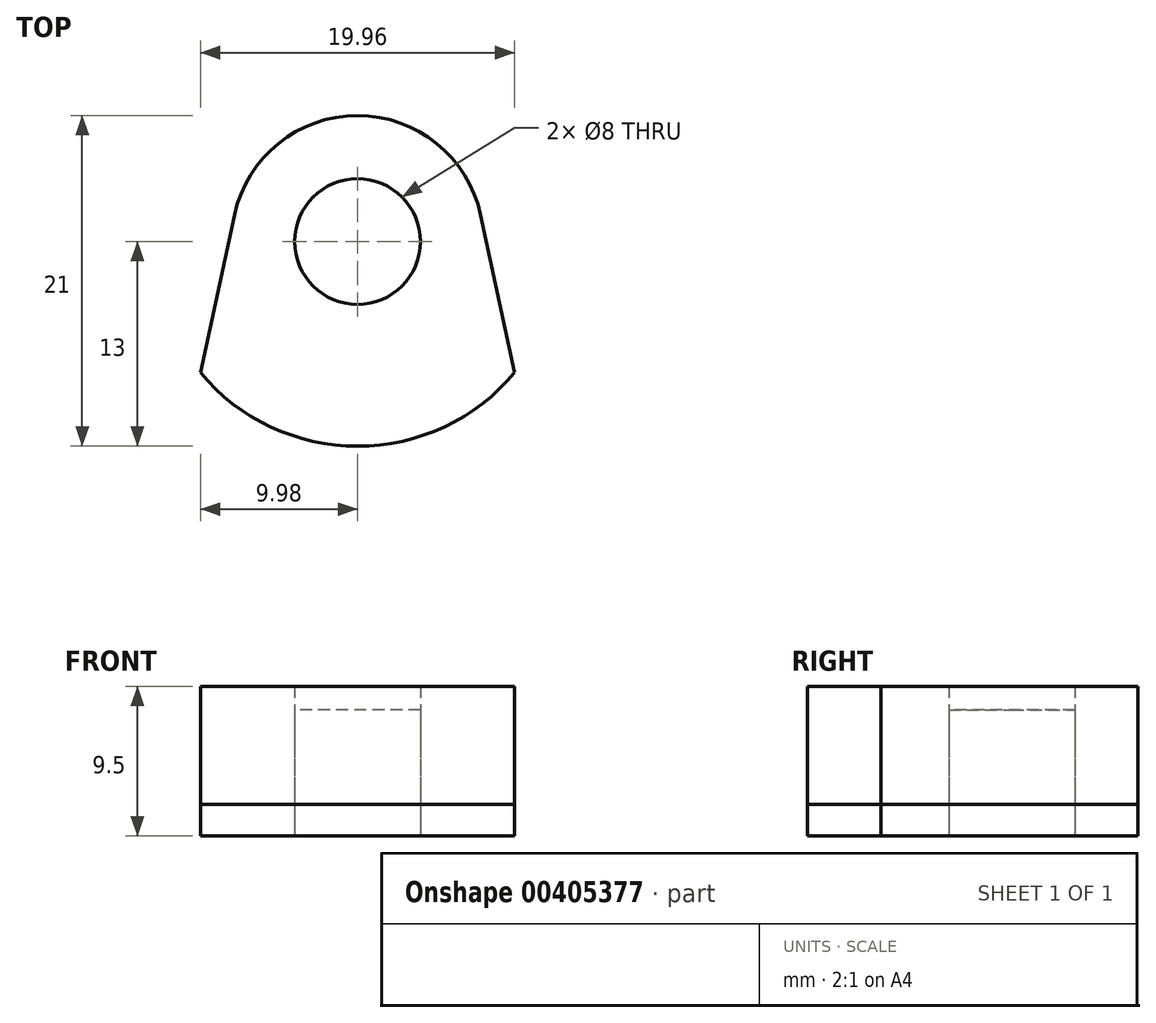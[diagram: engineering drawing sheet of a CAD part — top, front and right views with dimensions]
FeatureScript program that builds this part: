
annotation { "Feature Type Name" : "Feature", "Feature Type Description" : "" }
export const myFeature = defineFeature(function(context is Context, id is Id, definition is map)
    precondition{}
    {
        {
            var Q0;
            Q0=qCreatedBy(makeId("Top.planeOp"),FACE);
            var sketch = newSketch(context, id + "F0", { "sketchPlane" : qUnion([Q0])});
            skCircle(sketch, "E0", {"center": v(0, 0) * mm, "radius": 4 * mm});
            skArc(sketch, "E1", {"start": v(7.82, 1.69) * mm, "mid": v(0, 8) * mm, "end": v(-7.82, 1.69) * mm});
            skLineSegment(sketch, "E2", {"start": v(0, -20) * mm, "end": v(12.5, -20) * mm});
            skLineSegment(sketch, "E3", {"start": v(12.5, -20) * mm, "end": v(-12.5, -20) * mm});
            skLineSegment(sketch, "E4", {"start": v(-12.5, -20) * mm, "end": v(-7.82, 1.69) * mm});
            skLineSegment(sketch, "E5", {"start": v(12.5, -20) * mm, "end": v(7.82, 1.69) * mm});
            skArc(sketch, "E6", {"start": v(9.98, -8.33) * mm, "mid": v(0, -13) * mm, "end": v(-9.98, -8.33) * mm});
            skCircle(sketch, "E7", {"center": v(-7.79, -16.5) * mm, "radius": 2 * mm});
            skCircle(sketch, "E8.MirrorC", {"center": v(7.79, -16.5) * mm, "radius": 2 * mm});
            skSolve(sketch);
        }
        {
            var Q0;
            {var subQ3=sQuery(id+"F0.wireOp",EDGE,"E6");Q0=makeQuery(id+"F0.imprint","IMPRINT",FACE,{"disambiguationData":[TD([[makeQuery(id+"F0.imprint","IMPRINT",EDGE,{"derivedFrom":subQ3}),1.0]])]});}
            extrude(context, id + "F1", {"entities" : qUnion([Q0]), "depth" : 9.5 * mm});
        }
        {
            var Q0;
            Q0=makeQuery(id+"F0.imprint","IMPRINT",FACE,{"disambiguationData":[TD([[makeQuery(id+"F0.imprint","IMPRINT",EDGE,{"derivedFrom":sQuery(id+"F0.wireOp",EDGE,"E0")}),1.0]])]});
            extrude(context, id + "F2", {"entities" : qUnion([Q0]), "depth" : 8 * mm});
        }
        {
            var Q0;
            Q0=makeQuery(id+"F0.imprint","IMPRINT",FACE,{"disambiguationData":[TD([[makeQuery(id+"F0.imprint","IMPRINT",EDGE,{"derivedFrom":sQuery(id+"F0.wireOp",EDGE,"E0")}),-1.0]])]});
            extrude(context, id + "F3", {"entities" : qUnion([Q0]), "depth" : 2 * mm});
        }
    });
